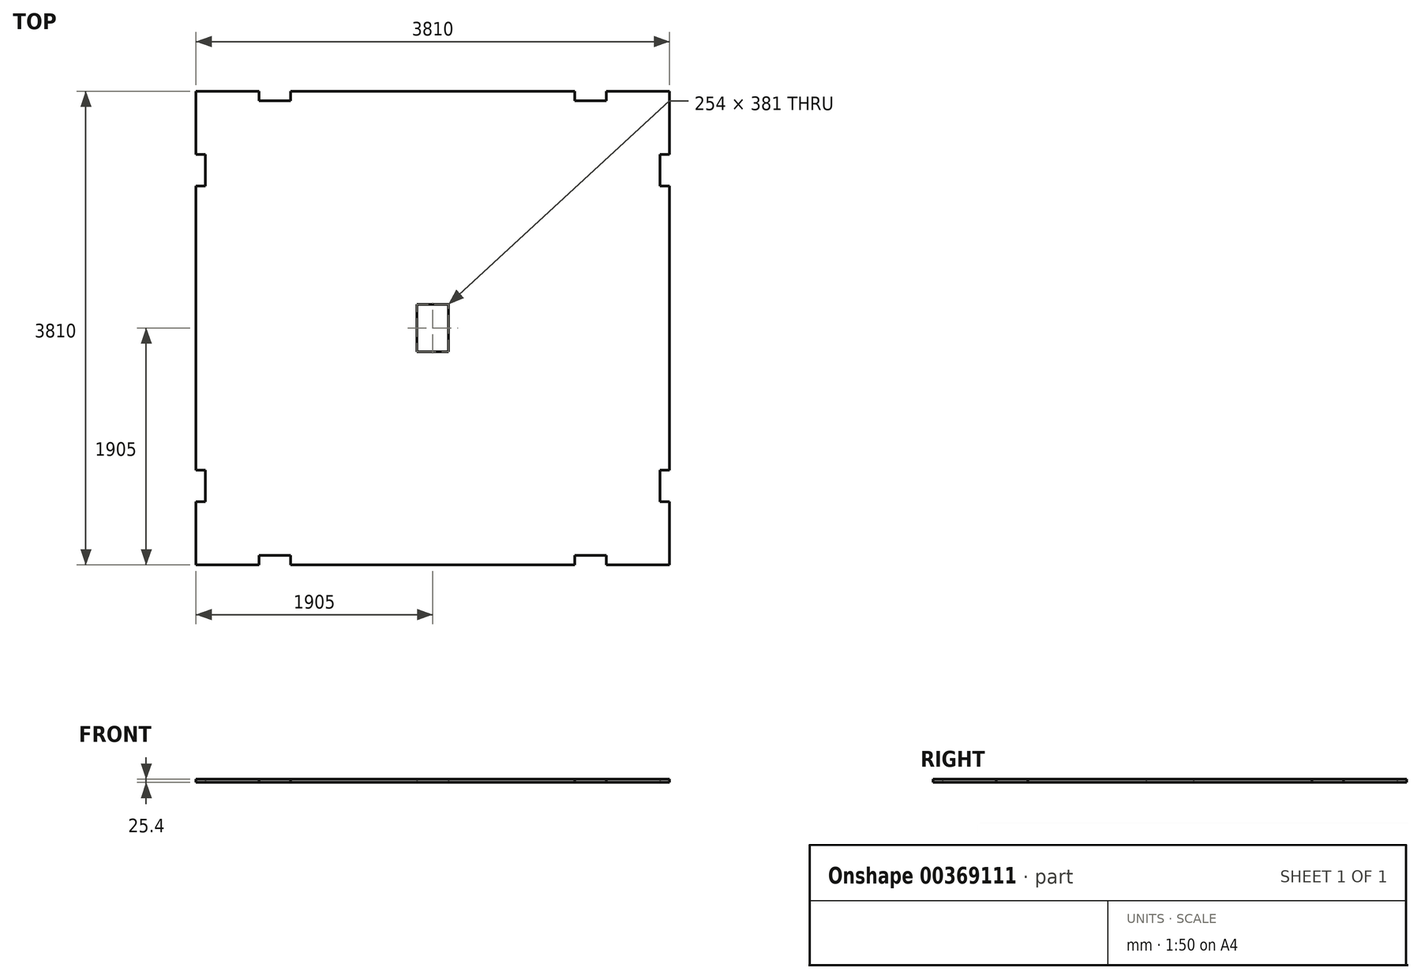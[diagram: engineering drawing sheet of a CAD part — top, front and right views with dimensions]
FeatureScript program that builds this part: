
annotation { "Feature Type Name" : "Feature", "Feature Type Description" : "" }
export const myFeature = defineFeature(function(context is Context, id is Id, definition is map)
    precondition{}
    {
        {
            var Q0;
            Q0=qCreatedBy(makeId("Top.planeOp"),FACE);
            var sketch = newSketch(context, id + "F0", { "sketchPlane" : qUnion([Q0])});
            skLineSegment(sketch, "E0.bottom", {"start": v(1905, 1905) * mm, "end": v(1397, 1905) * mm});
            skLineSegment(sketch, "E0.top", {"start": v(1143, -1905) * mm, "end": v(-1143, -1905) * mm});
            skLineSegment(sketch, "E0.left", {"start": v(1905, 1905) * mm, "end": v(1905, 1397) * mm});
            skLineSegment(sketch, "E0.right", {"start": v(-1905, 1905) * mm, "end": v(-1905, 1397) * mm});
            skPoint(sketch, "E0.middle", {"position": v(0, 0) * mm});
            skLineSegment(sketch, "E1", {"start": v(-1828.8, 1397) * mm, "end": v(-1828.8, 1397) * mm});
            skLineSegment(sketch, "E2.trimOffspring", {"start": v(-1905, 1143) * mm, "end": v(-1905, -1143) * mm});
            skLineSegment(sketch, "E3", {"start": v(-1905, 1905) * mm, "end": v(-1397, 1905) * mm});
            skLineSegment(sketch, "E4", {"start": v(-1397, 1905) * mm, "end": v(-1397, 1828.8) * mm});
            skLineSegment(sketch, "E5", {"start": v(-1397, 1828.8) * mm, "end": v(-1143, 1828.8) * mm});
            skLineSegment(sketch, "E6", {"start": v(-1143, 1905) * mm, "end": v(-1143, 1828.8) * mm});
            skLineSegment(sketch, "E7", {"start": v(-1905, -1905) * mm, "end": v(-1905, -1397) * mm});
            skLineSegment(sketch, "E8", {"start": v(-1905, -1397) * mm, "end": v(-1828.8, -1397) * mm});
            skLineSegment(sketch, "E9", {"start": v(-1905, -1143) * mm, "end": v(-1828.8, -1143) * mm});
            skLineSegment(sketch, "E10", {"start": v(-1828.8, -1143) * mm, "end": v(-1828.8, -1397) * mm});
            skLineSegment(sketch, "E11", {"start": v(-1905, -1905) * mm, "end": v(-1397, -1905) * mm});
            skLineSegment(sketch, "E12", {"start": v(-1397, -1905) * mm, "end": v(-1397, -1828.8) * mm});
            skLineSegment(sketch, "E13", {"start": v(-1397, -1828.8) * mm, "end": v(-1143, -1828.8) * mm});
            skLineSegment(sketch, "E14", {"start": v(-1143, -1828.8) * mm, "end": v(-1143, -1905) * mm});
            skLineSegment(sketch, "E15.trimOffspring", {"start": v(-1397, -1905) * mm, "end": v(-1905, -1905) * mm});
            skLineSegment(sketch, "E16", {"start": v(1905, -1905) * mm, "end": v(1397, -1905) * mm});
            skLineSegment(sketch, "E17", {"start": v(1397, -1905) * mm, "end": v(1397, -1828.8) * mm});
            skLineSegment(sketch, "E18", {"start": v(1397, -1828.8) * mm, "end": v(1143, -1828.8) * mm});
            skLineSegment(sketch, "E19", {"start": v(1143, -1828.8) * mm, "end": v(1143, -1905) * mm});
            skLineSegment(sketch, "E20", {"start": v(1905, -1905) * mm, "end": v(1905, -1397) * mm});
            skLineSegment(sketch, "E21", {"start": v(1905, -1397) * mm, "end": v(1828.8, -1397) * mm});
            skLineSegment(sketch, "E22", {"start": v(1828.8, -1397) * mm, "end": v(1828.8, -1143) * mm});
            skLineSegment(sketch, "E23", {"start": v(1828.8, -1143) * mm, "end": v(1905, -1143) * mm});
            skLineSegment(sketch, "E24.trimOffspring", {"start": v(1905, -1397) * mm, "end": v(1905, -1905) * mm});
            skLineSegment(sketch, "E25", {"start": v(1905, 1397) * mm, "end": v(1828.8, 1397) * mm});
            skLineSegment(sketch, "E26", {"start": v(1828.8, 1397) * mm, "end": v(1828.8, 1143) * mm});
            skLineSegment(sketch, "E27", {"start": v(1905, 1143) * mm, "end": v(1828.8, 1143) * mm});
            skLineSegment(sketch, "E28.trimOffspring", {"start": v(1905, 1143) * mm, "end": v(1905, -1143) * mm});
            skLineSegment(sketch, "E29", {"start": v(1397, 1905) * mm, "end": v(1397, 1828.8) * mm});
            skLineSegment(sketch, "E30", {"start": v(1143, 1905) * mm, "end": v(1143, 1828.8) * mm});
            skLineSegment(sketch, "E31", {"start": v(1397, 1828.8) * mm, "end": v(1143, 1828.8) * mm});
            skLineSegment(sketch, "E32.trimOffspring", {"start": v(1143, 1905) * mm, "end": v(-1143, 1905) * mm});
            skLineSegment(sketch, "E33.trimOffspring", {"start": v(-1905, -1397) * mm, "end": v(-1905, -1905) * mm});
            skPoint(sketch, "E34.top.start.orphan", {"position": v(-254, 635) * mm});
            skPoint(sketch, "E34.right.end.orphan", {"position": v(254, 635) * mm});
            skPoint(sketch, "E34.bottom.end.orphan", {"position": v(254, -635) * mm});
            skPoint(sketch, "E34.bottom.start.orphan", {"position": v(-254, -635) * mm});
            skLineSegment(sketch, "E35.trimOffspring", {"start": v(-1397, 1905) * mm, "end": v(-1905, 1905) * mm});
            skLineSegment(sketch, "E36.bottom", {"start": v(127, 190.5) * mm, "end": v(-127, 190.5) * mm});
            skLineSegment(sketch, "E36.top", {"start": v(127, -190.5) * mm, "end": v(-127, -190.5) * mm});
            skLineSegment(sketch, "E36.left", {"start": v(127, 190.5) * mm, "end": v(127, -190.5) * mm});
            skLineSegment(sketch, "E36.right", {"start": v(-127, 190.5) * mm, "end": v(-127, -190.5) * mm});
            skLineSegment(sketch, "E37", {"start": v(-1905, 1397) * mm, "end": v(-1828.8, 1397) * mm});
            skLineSegment(sketch, "E38", {"start": v(-1828.8, 1397) * mm, "end": v(-1828.8, 1143) * mm});
            skLineSegment(sketch, "E39", {"start": v(-1828.8, 1143) * mm, "end": v(-1905, 1143) * mm});
            skSolve(sketch);
        }
        {
            var Q0;
            Q0=makeQuery(id+"F0.imprint","IMPRINT",FACE,{"disambiguationData":[TD([[makeQuery(id+"F0.imprint","IMPRINT",EDGE,{"derivedFrom":sQuery(id+"F0.wireOp",EDGE,"E0.top")}),-1.0]])]});
            extrude(context, id + "F1", {"entities" : qUnion([Q0]), "depth" : 25.4 * mm});
        }
    });
